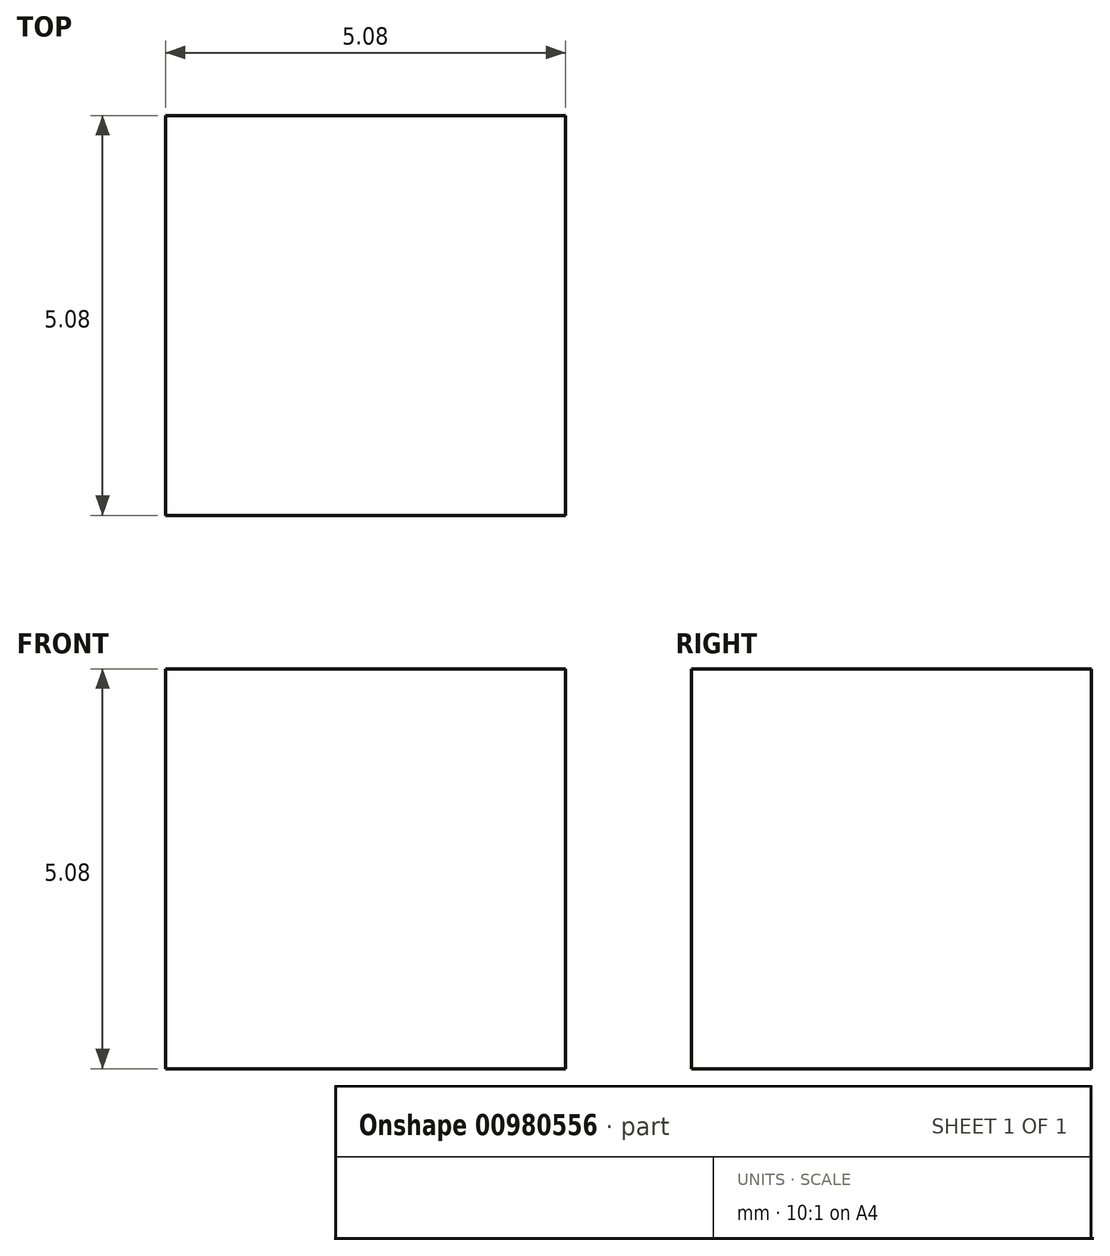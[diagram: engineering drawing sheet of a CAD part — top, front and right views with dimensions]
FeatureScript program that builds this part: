
annotation { "Feature Type Name" : "Feature", "Feature Type Description" : "" }
export const myFeature = defineFeature(function(context is Context, id is Id, definition is map)
    precondition{}
    {
        {
            var Q0;
            Q0=qCreatedBy(makeId("Top.planeOp"),FACE);
            var sketch = newSketch(context, id + "F0", { "sketchPlane" : qUnion([Q0])});
            skLineSegment(sketch, "E0.bottom", {"start": v(2.54, -2.54) * mm, "end": v(-2.54, -2.54) * mm});
            skLineSegment(sketch, "E0.top", {"start": v(2.54, 2.54) * mm, "end": v(-2.54, 2.54) * mm});
            skLineSegment(sketch, "E0.left", {"start": v(2.54, -2.54) * mm, "end": v(2.54, 2.54) * mm});
            skLineSegment(sketch, "E0.right", {"start": v(-2.54, -2.54) * mm, "end": v(-2.54, 2.54) * mm});
            skPoint(sketch, "E0.middle", {"position": v(0, 0) * mm});
            skSolve(sketch);
        }
        {
            var Q0;
            Q0=makeQuery(id+"F0.imprint","IMPRINT",FACE,{"disambiguationData":[TD([[makeQuery(id+"F0.imprint","IMPRINT",EDGE,{"derivedFrom":sQuery(id+"F0.wireOp",EDGE,"E0.bottom")}),-1.0]])]});
            extrude(context, id + "F1", {"entities" : qUnion([Q0]), "depth" : 5.08 * mm, "offsetDistance" : 25.4 * mm});
        }
    });
